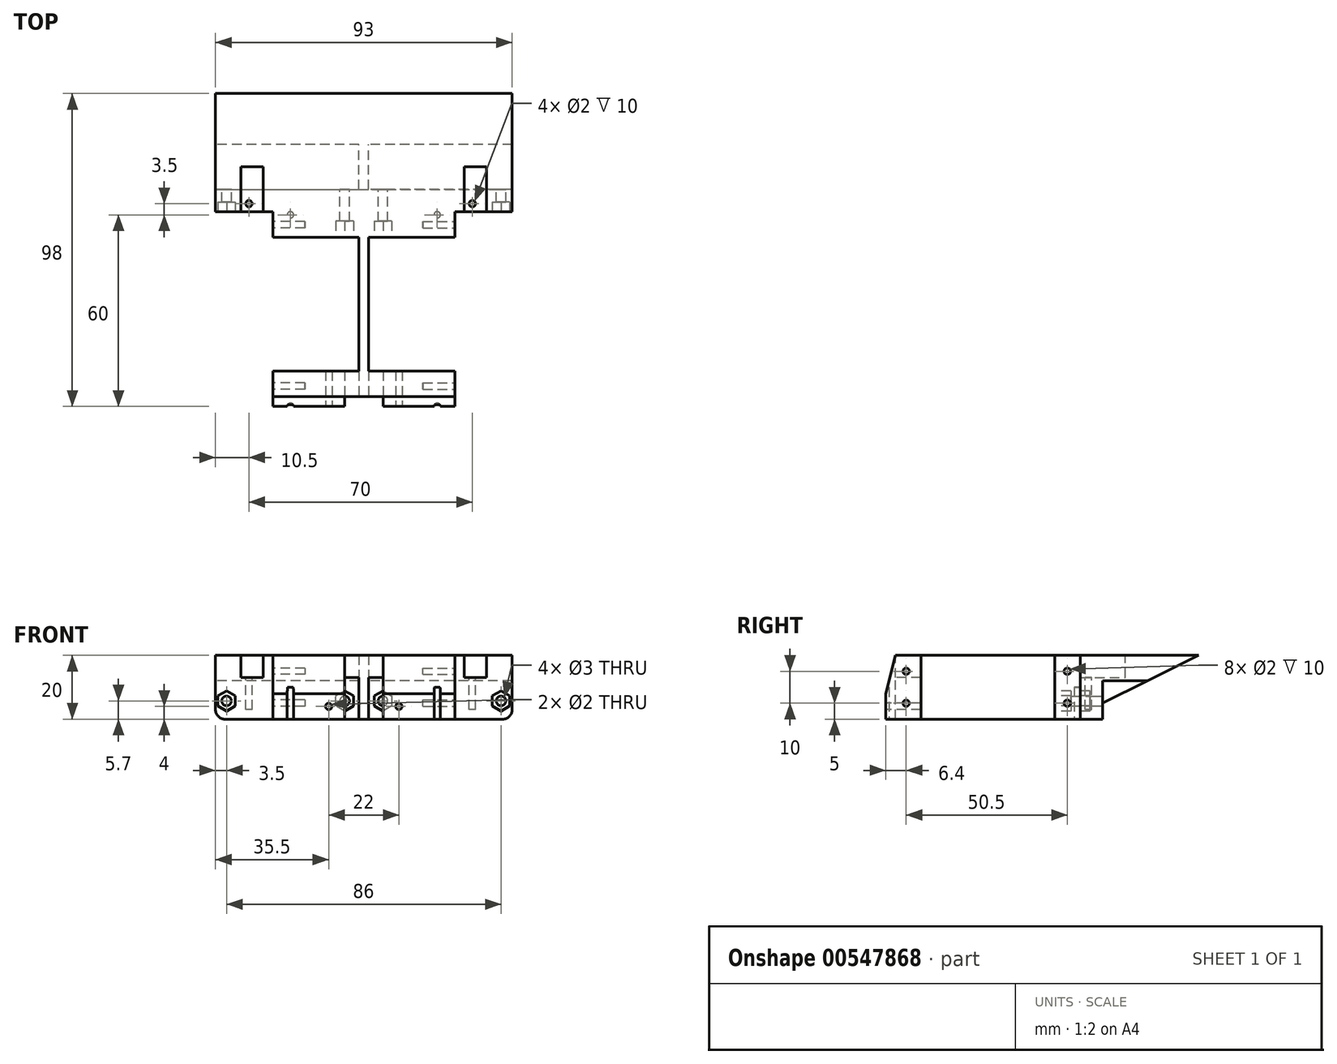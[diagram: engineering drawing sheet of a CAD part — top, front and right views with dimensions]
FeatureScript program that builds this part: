
annotation { "Feature Type Name" : "Feature", "Feature Type Description" : "" }
export const myFeature = defineFeature(function(context is Context, id is Id, definition is map)
    precondition{}
    {
        {
            var Q0;
            Q0=qCreatedBy(makeId("Top.planeOp"),FACE);
            var sketch = newSketch(context, id + "F0", { "sketchPlane" : qUnion([Q0])});
            skLineSegment(sketch, "E0", {"start": v(0, 0) * mm, "end": v(0, 8) * mm});
            skLineSegment(sketch, "E1", {"start": v(0, 8) * mm, "end": v(27, 8) * mm});
            skLineSegment(sketch, "E2", {"start": v(27, 8) * mm, "end": v(27, 50) * mm});
            skLineSegment(sketch, "E3", {"start": v(27, 50) * mm, "end": v(0, 50) * mm});
            skLineSegment(sketch, "E4", {"start": v(0, 50) * mm, "end": v(0, 65) * mm});
            skLineSegment(sketch, "E5", {"start": v(0, 65) * mm, "end": v(57, 65) * mm});
            skLineSegment(sketch, "E6", {"start": v(57, 65) * mm, "end": v(57, 50) * mm});
            skLineSegment(sketch, "E7", {"start": v(57, 50) * mm, "end": v(30, 50) * mm});
            skLineSegment(sketch, "E8", {"start": v(30, 50) * mm, "end": v(30, 8) * mm});
            skLineSegment(sketch, "E9", {"start": v(30, 8) * mm, "end": v(57, 8) * mm});
            skLineSegment(sketch, "E10", {"start": v(57, 8) * mm, "end": v(57, 0) * mm});
            skLineSegment(sketch, "E11", {"start": v(57, 0) * mm, "end": v(0, 0) * mm});
            skSolve(sketch);
        }
        {
            var Q0;
            Q0=makeQuery(id+"F0.imprint","IMPRINT",FACE,{"disambiguationData":[TD([[makeQuery(id+"F0.imprint","IMPRINT",EDGE,{"derivedFrom":sQuery(id+"F0.wireOp",EDGE,"E0")}),-1.0]])]});
            extrude(context, id + "F1", {"entities" : qUnion([Q0]), "depth" : 20 * mm, "offsetDistance" : 25 * mm});
        }
        {
            var Q0;
            Q0=makeQuery(id+"F1.opExtrude","SWEPT_FACE",FACE,{"disambiguationData":[OSD([sQuery(id+"F0.wireOp",EDGE,"E10")])]});
            var sketch = newSketch(context, id + "F2", { "sketchPlane" : qUnion([Q0])});
            skCircle(sketch, "E12", {"center": v(3.4, 15) * mm, "radius": 1 * mm});
            skCircle(sketch, "E13", {"center": v(3.4, 5) * mm, "radius": 1 * mm});
            skCircle(sketch, "E14", {"center": v(53.9, 15) * mm, "radius": 1 * mm});
            skCircle(sketch, "E15", {"center": v(53.9, 5) * mm, "radius": 1 * mm});
            skLineSegment(sketch, "E16", {"start": v(53.9, 5) * mm, "end": v(3.4, 5) * mm, "construction": true});
            skLineSegment(sketch, "E17", {"start": v(53.9, 5) * mm, "end": v(53.9, 15) * mm, "construction": true});
            skLineSegment(sketch, "E18", {"start": v(3.4, 5) * mm, "end": v(3.4, 15) * mm, "construction": true});
            skSolve(sketch);
        }
        {
            var Q0;
            Q0=makeQuery(id+"F2.imprint","IMPRINT",FACE,{"disambiguationData":[TD([[makeQuery(id+"F2.imprint","IMPRINT",EDGE,{"derivedFrom":sQuery(id+"F2.wireOp",EDGE,"E12")}),1.0]])]});
            var Q1;
            Q1=makeQuery(id+"F2.imprint","IMPRINT",FACE,{"disambiguationData":[TD([[makeQuery(id+"F2.imprint","IMPRINT",EDGE,{"derivedFrom":sQuery(id+"F2.wireOp",EDGE,"E13")}),1.0]])]});
            var Q2;
            Q2=makeQuery(id+"F2.imprint","IMPRINT",FACE,{"disambiguationData":[TD([[makeQuery(id+"F2.imprint","IMPRINT",EDGE,{"derivedFrom":sQuery(id+"F2.wireOp",EDGE,"E14")}),1.0]])]});
            var Q3;
            Q3=makeQuery(id+"F2.imprint","IMPRINT",FACE,{"disambiguationData":[TD([[makeQuery(id+"F2.imprint","IMPRINT",EDGE,{"derivedFrom":sQuery(id+"F2.wireOp",EDGE,"E15")}),1.0]])]});
            extrude(context, id + "F3", {"entities" : qUnion([Q0, Q1, Q2, Q3]), "operationType" : NewBodyOperationType.REMOVE, "oppositeDirection" : true, "depth" : 10 * mm, "offsetDistance" : 25 * mm});
        }
        {
            var Q0;
            Q0=makeQuery(id+"F1.opExtrude","SWEPT_FACE",FACE,{"disambiguationData":[OSD([sQuery(id+"F0.wireOp",EDGE,"E4")])]});
            var sketch = newSketch(context, id + "F4", { "sketchPlane" : qUnion([Q0])});
            skCircle(sketch, "E19", {"center": v(-53.9, 15) * mm, "radius": 1 * mm});
            skCircle(sketch, "E20", {"center": v(-53.9, 5) * mm, "radius": 1 * mm});
            skCircle(sketch, "E21", {"center": v(-3.4, 15) * mm, "radius": 1 * mm});
            skCircle(sketch, "E22", {"center": v(-3.4, 5) * mm, "radius": 1 * mm});
            skSolve(sketch);
        }
        {
            var Q0;
            Q0=makeQuery(id+"F4.imprint","IMPRINT",FACE,{"disambiguationData":[TD([[makeQuery(id+"F4.imprint","IMPRINT",EDGE,{"derivedFrom":sQuery(id+"F4.wireOp",EDGE,"E19")}),1.0]])]});
            var Q1;
            Q1=makeQuery(id+"F4.imprint","IMPRINT",FACE,{"disambiguationData":[TD([[makeQuery(id+"F4.imprint","IMPRINT",EDGE,{"derivedFrom":sQuery(id+"F4.wireOp",EDGE,"E20")}),1.0]])]});
            var Q2;
            Q2=makeQuery(id+"F4.imprint","IMPRINT",FACE,{"disambiguationData":[TD([[makeQuery(id+"F4.imprint","IMPRINT",EDGE,{"derivedFrom":sQuery(id+"F4.wireOp",EDGE,"E21")}),1.0]])]});
            var Q3;
            Q3=makeQuery(id+"F4.imprint","IMPRINT",FACE,{"disambiguationData":[TD([[makeQuery(id+"F4.imprint","IMPRINT",EDGE,{"derivedFrom":sQuery(id+"F4.wireOp",EDGE,"E22")}),1.0]])]});
            extrude(context, id + "F5", {"entities" : qUnion([Q0, Q1, Q2, Q3]), "operationType" : NewBodyOperationType.REMOVE, "oppositeDirection" : true, "depth" : 10 * mm, "offsetDistance" : 25 * mm});
        }
        {
            var Q0;
            Q0=makeQuery(id+"F1.opExtrude","SWEPT_FACE",FACE,{"disambiguationData":[OSD([sQuery(id+"F0.wireOp",EDGE,"E6")])]});
            var sketch = newSketch(context, id + "F6", { "sketchPlane" : qUnion([Q0])});
            skLineSegment(sketch, "E23", {"start": v(65, 5) * mm, "end": v(95, 20) * mm});
            skLineSegment(sketch, "E24", {"start": v(95, 20) * mm, "end": v(65, 20) * mm});
            skLineSegment(sketch, "E25", {"start": v(65, 20) * mm, "end": v(65, 5) * mm});
            skSolve(sketch);
        }
        {
            var Q0;
            Q0=makeQuery(id+"F6.imprint","IMPRINT",FACE,{"disambiguationData":[TD([[makeQuery(id+"F6.imprint","IMPRINT",EDGE,{"derivedFrom":sQuery(id+"F6.wireOp",EDGE,"E23")}),1.0]])]});
            var Q1;
            Q1=makeQuery(id+"F1.opExtrude","SWEPT_FACE",FACE,{"disambiguationData":[OSD([sQuery(id+"F0.wireOp",EDGE,"E4")])]});
            extrude(context, id + "F7", {"entities" : qUnion([Q0]), "operationType" : NewBodyOperationType.ADD, "oppositeDirection" : true, "depth" : 75 * mm, "endBoundEntityFace" : qUnion([Q1]), "offsetDistance" : 25 * mm, "hasSecondDirection" : true, "secondDirectionOppositeDirection" : true, "secondDirectionDepth" : -18 * mm});
        }
        {
            var Q0;
            Q0=makeQuery(id+"F1.opExtrude","SWEPT_FACE",FACE,{"disambiguationData":[OSD([sQuery(id+"F0.wireOp",EDGE,"E11")])]});
            var sketch = newSketch(context, id + "F8", { "sketchPlane" : qUnion([Q0])});
            skLineSegment(sketch, "E26.bottom", {"start": v(27, 13) * mm, "end": v(22.5, 13) * mm});
            skLineSegment(sketch, "E27", {"start": v(28.5, 0) * mm, "end": v(28.5, 20) * mm, "construction": true});
            skLineSegment(sketch, "E28", {"start": v(18, 10) * mm, "end": v(28.5, 10) * mm, "construction": true});
            skLineSegment(sketch, "E29", {"start": v(22.5, 7) * mm, "end": v(22.5, 0) * mm});
            skLineSegment(sketch, "E30", {"start": v(22.5, 0) * mm, "end": v(27, 0) * mm});
            skLineSegment(sketch, "E31", {"start": v(27, 0) * mm, "end": v(27, 13) * mm});
            skLineSegment(sketch, "E32.MirrorCS", {"start": v(34.5, 7) * mm, "end": v(34.5, 0) * mm});
            skLineSegment(sketch, "E33.MirrorCS", {"start": v(34.5, 0) * mm, "end": v(30, 0) * mm});
            skLineSegment(sketch, "E34.MirrorCS", {"start": v(30, 0) * mm, "end": v(30, 13) * mm});
            skLineSegment(sketch, "E35.MirrorCS", {"start": v(30, 13) * mm, "end": v(34.5, 13) * mm});
            skLineSegment(sketch, "E36", {"start": v(34.5, 7) * mm, "end": v(34.5, 13) * mm});
            skLineSegment(sketch, "E37", {"start": v(22.5, 13) * mm, "end": v(22.5, 7) * mm});
            skPoint(sketch, "E38.orphan", {"position": v(18, 7) * mm});
            skPoint(sketch, "E26.right.start.orphan", {"position": v(18, 13) * mm});
            skPoint(sketch, "E39.orphan", {"position": v(39, 13) * mm});
            skPoint(sketch, "E40.MirrorCS.end.orphan", {"position": v(39, 7) * mm});
            skPoint(sketch, "E41.MirrorCS.start.orphan", {"position": v(34.5, 7) * mm});
            skSolve(sketch);
        }
        {
            var Q0;
            Q0=makeQuery(id+"F8.imprint","IMPRINT",FACE,{"disambiguationData":[TD([[makeQuery(id+"F8.imprint","IMPRINT",EDGE,{"derivedFrom":sQuery(id+"F8.wireOp",EDGE,"E26.bottom")}),1.0]])]});
            var Q1;
            Q1=makeQuery(id+"F8.imprint","IMPRINT",FACE,{"disambiguationData":[TD([[makeQuery(id+"F8.imprint","IMPRINT",EDGE,{"derivedFrom":sQuery(id+"F8.wireOp",EDGE,"E32.MirrorCS")}),-1.0]])]});
            extrude(context, id + "F9", {"entities" : qUnion([Q0, Q1]), "operationType" : NewBodyOperationType.REMOVE, "oppositeDirection" : true, "depth" : 12 * mm, "offsetDistance" : 25 * mm});
        }
        {
            var Q0;
            Q0=makeQuery(id+"F1.opExtrude","CAP_FACE",FACE,{"disambiguationData":[OSD([sQuery(id+"F0.wireOp",EDGE,"E0"),sQuery(id+"F0.wireOp",EDGE,"E1"),sQuery(id+"F0.wireOp",EDGE,"E2"),sQuery(id+"F0.wireOp",EDGE,"E3"),sQuery(id+"F0.wireOp",EDGE,"E4"),sQuery(id+"F0.wireOp",EDGE,"E5"),sQuery(id+"F0.wireOp",EDGE,"E6"),sQuery(id+"F0.wireOp",EDGE,"E7"),sQuery(id+"F0.wireOp",EDGE,"E8"),sQuery(id+"F0.wireOp",EDGE,"E9"),sQuery(id+"F0.wireOp",EDGE,"E10"),sQuery(id+"F0.wireOp",EDGE,"E11")])],"isStart":true});
            var sketch = newSketch(context, id + "F10", { "sketchPlane" : qUnion([Q0])});
            skLineSegment(sketch, "E42", {"start": v(30, -65) * mm, "end": v(30, -105) * mm});
            skLineSegment(sketch, "E43", {"start": v(30, -105) * mm, "end": v(80, -105) * mm});
            skLineSegment(sketch, "E44", {"start": v(80, -105) * mm, "end": v(80, -65) * mm});
            skLineSegment(sketch, "E45", {"start": v(80, -65) * mm, "end": v(30, -65) * mm});
            skLineSegment(sketch, "E46", {"start": v(27, -50) * mm, "end": v(30, -50) * mm, "construction": true});
            skLineSegment(sketch, "E47", {"start": v(28.5, -50) * mm, "end": v(28.5, -54.4) * mm, "construction": true});
            skLineSegment(sketch, "E48.MirrorCS", {"start": v(27, -65) * mm, "end": v(27, -105) * mm});
            skLineSegment(sketch, "E49.MirrorCS", {"start": v(-23, -65) * mm, "end": v(27, -65) * mm});
            skLineSegment(sketch, "E50.MirrorCS", {"start": v(-23, -105) * mm, "end": v(-23, -65) * mm});
            skLineSegment(sketch, "E51.MirrorCS", {"start": v(27, -105) * mm, "end": v(-23, -105) * mm});
            skSolve(sketch);
        }
        {
            var Q0;
            {var subQ3=sQuery(id+"F10.wireOp",EDGE,"E48.MirrorCS");Q0=makeQuery(id+"F10.imprint","IMPRINT",FACE,{"disambiguationData":[TD([[makeQuery(id+"F10.imprint","IMPRINT",EDGE,{"derivedFrom":subQ3}),-1.0]])]});}
            var Q1;
            {var subQ4=sQuery(id+"F10.wireOp",EDGE,"E42");Q1=makeQuery(id+"F10.imprint","IMPRINT",FACE,{"disambiguationData":[TD([[makeQuery(id+"F10.imprint","IMPRINT",EDGE,{"derivedFrom":subQ4}),1.0]])]});}
            extrude(context, id + "F11", {"entities" : qUnion([Q0, Q1]), "operationType" : NewBodyOperationType.REMOVE, "oppositeDirection" : true, "depth" : 12 * mm, "offsetDistance" : 25 * mm});
        }
        {
            var Q0;
            Q0=makeQuery(id+"F11.boolean.opBoolean","MERGE",FACE,{"derivedFrom":[makeQuery(id+"F1.opExtrude","SWEPT_FACE",FACE,{"disambiguationData":[OSD([sQuery(id+"F0.wireOp",EDGE,"E5")])]}),makeQuery(id+"F11.opExtrude","SWEPT_FACE",FACE,{"disambiguationData":[OSD([sQuery(id+"F10.wireOp",EDGE,"E45")])]}),makeQuery(id+"F11.opExtrude","SWEPT_FACE",FACE,{"disambiguationData":[OSD([sQuery(id+"F10.wireOp",EDGE,"E49.MirrorCS")])]})]});
            var sketch = newSketch(context, id + "F12", { "sketchPlane" : qUnion([Q0])});
            skLineSegment(sketch, "E52", {"start": v(-75, 0) * mm, "end": v(-75, 20) * mm});
            skLineSegment(sketch, "E53", {"start": v(-75, 20) * mm, "end": v(-57, 20) * mm});
            skLineSegment(sketch, "E54", {"start": v(-57, 20) * mm, "end": v(-57, 0) * mm});
            skLineSegment(sketch, "E55", {"start": v(-57, 0) * mm, "end": v(0, 0) * mm, "construction": true});
            skLineSegment(sketch, "E56", {"start": v(-28.5, 0) * mm, "end": v(-28.5, 25.91) * mm, "construction": true});
            skLineSegment(sketch, "E57", {"start": v(-57, 0) * mm, "end": v(-75, 0) * mm});
            skLineSegment(sketch, "E58.MirrorCS", {"start": v(0, 0) * mm, "end": v(18, 0) * mm});
            skLineSegment(sketch, "E59.MirrorCS", {"start": v(0, 20) * mm, "end": v(0, 0) * mm});
            skLineSegment(sketch, "E60.MirrorCS", {"start": v(18, 20) * mm, "end": v(0, 20) * mm});
            skLineSegment(sketch, "E61.MirrorCS", {"start": v(18, 0) * mm, "end": v(18, 20) * mm});
            skSolve(sketch);
        }
        {
            var Q0;
            Q0=makeQuery(id+"F12.imprint","IMPRINT",FACE,{"disambiguationData":[TD([[makeQuery(id+"F12.imprint","IMPRINT",EDGE,{"derivedFrom":sQuery(id+"F12.wireOp",EDGE,"E52")}),-1.0]])]});
            var Q1;
            Q1=makeQuery(id+"F12.imprint","IMPRINT",FACE,{"disambiguationData":[TD([[makeQuery(id+"F12.imprint","IMPRINT",EDGE,{"derivedFrom":sQuery(id+"F12.wireOp",EDGE,"E58.MirrorCS")}),1.0]])]});
            extrude(context, id + "F13", {"entities" : qUnion([Q0, Q1]), "operationType" : NewBodyOperationType.ADD, "oppositeDirection" : true, "depth" : 7 * mm, "offsetDistance" : 25 * mm});
        }
        {
            var Q0;
            Q0=makeQuery(id+"F13.boolean.opBoolean","MERGE",FACE,{"derivedFrom":[makeQuery(id+"FaigYpugeFjXcMo_1.boolean.opBoolean","MERGE",FACE,{"derivedFrom":[makeQuery(id+"F11.boolean.opBoolean","COPY",FACE,{"derivedFrom":makeQuery(id+"F11.opExtrude","SWEPT_FACE",FACE,{"disambiguationData":[OSD([sQuery(id+"F10.wireOp",EDGE,"E45")])]})}),makeQuery(id+"FaigYpugeFjXcMo_1.opExtrude","SWEPT_FACE",FACE,{"disambiguationData":[OSD([sQuery(id+"Fybsm6U9hBihCkf_1.wireOp",EDGE,"Q4yo8pTs-f2aV-JBux-9yHL-tDEv9YkHMdLA.bottom")])]})]}),makeQuery(id+"F13.opExtrude","CAP_FACE",FACE,{"disambiguationData":[OSD([sQuery(id+"F12.wireOp",EDGE,"E52"),sQuery(id+"F12.wireOp",EDGE,"E53"),sQuery(id+"F12.wireOp",EDGE,"E54"),sQuery(id+"F12.wireOp",EDGE,"E57")])],"isStart":true})]});
            var sketch = newSketch(context, id + "F14", { "sketchPlane" : qUnion([Q0])});
            skCircle(sketch, "E62", {"center": v(-71.5, 5.7) * mm, "radius": 1.5 * mm});
            skLineSegment(sketch, "E63", {"start": v(-71.5, 5.7) * mm, "end": v(-34.5, 5.7) * mm, "construction": true});
            skCircle(sketch, "E64", {"center": v(-34.5, 5.7) * mm, "radius": 1.5 * mm});
            skLineSegment(sketch, "E65", {"start": v(-75, 0) * mm, "end": v(18, 0) * mm, "construction": true});
            skLineSegment(sketch, "E66", {"start": v(-28.5, 0) * mm, "end": v(-28.5, -6.25) * mm, "construction": true});
            skCircle(sketch, "E67.MirrorC", {"center": v(-22.5, 5.7) * mm, "radius": 1.5 * mm});
            skCircle(sketch, "E68.MirrorC", {"center": v(14.5, 5.7) * mm, "radius": 1.5 * mm});
            skSolve(sketch);
        }
        {
            var Q0;
            Q0 = qSketchRegion(id + "F14", true);
            extrude(context, id + "F15", {"entities" : qUnion([Q0]), "operationType" : NewBodyOperationType.REMOVE, "oppositeDirection" : true, "depth" : 25 * mm, "offsetDistance" : 25 * mm});
        }
        {
            var Q0;
            Q0=makeQuery(id+"F13.opExtrude","SWEPT_EDGE",EDGE,{"disambiguationData":[OSD([sQuery(id+"F12.wireOp",EDGE,"E52"),sQuery(id+"F12.wireOp",EDGE,"E57")])]});
            var Q1;
            Q1=makeQuery(id+"F13.opExtrude","SWEPT_EDGE",EDGE,{"disambiguationData":[OSD([sQuery(id+"F12.wireOp",EDGE,"E58.MirrorCS"),sQuery(id+"F12.wireOp",EDGE,"E61.MirrorCS")])]});
            fillet(context, id + "F16", {"entities" : qUnion([Q0, Q1]), "radius" : 3 * mm, "tangentPropagation" : true, "allowEdgeOverflow" : false});
        }
        {
            var Q0;
            Q0=makeQuery(id+"F1.opExtrude","SWEPT_FACE",FACE,{"disambiguationData":[OSD([sQuery(id+"F0.wireOp",EDGE,"E10")])]});
            var sketch = newSketch(context, id + "F17", { "sketchPlane" : qUnion([Q0])});
            skLineSegment(sketch, "E69", {"start": v(-3, 0) * mm, "end": v(0, 0) * mm});
            skLineSegment(sketch, "E70", {"start": v(0, 0) * mm, "end": v(0, 20) * mm});
            skLineSegment(sketch, "E71", {"start": v(-3, 0) * mm, "end": v(-3, 8) * mm});
            skLineSegment(sketch, "E72", {"start": v(-3, 8) * mm, "end": v(0, 20) * mm});
            skSolve(sketch);
        }
        {
            var Q0;
            Q0 = qSketchRegion(id + "F17", true);
            var Q1;
            Q1=makeQuery(id+"F9.boolean.opBoolean","COPY",FACE,{"derivedFrom":makeQuery(id+"F9.opExtrude","SWEPT_FACE",FACE,{"disambiguationData":[OSD([sQuery(id+"F8.wireOp",EDGE,"E32.MirrorCS"),sQuery(id+"F8.wireOp",EDGE,"E36")])]})});
            extrude(context, id + "F18", {"entities" : qUnion([Q0]), "operationType" : NewBodyOperationType.ADD, "endBound" : BoundingType.UP_TO_SURFACE, "oppositeDirection" : true, "depth" : 25 * mm, "endBoundEntityFace" : qUnion([Q1]), "offsetDistance" : 25 * mm});
        }
        {
            var Q0;
            Q0=makeQuery(id+"F1.opExtrude","SWEPT_FACE",FACE,{"disambiguationData":[OSD([sQuery(id+"F0.wireOp",EDGE,"E0")])]});
            var sketch = newSketch(context, id + "F19", { "sketchPlane" : qUnion([Q0])});
            skLineSegment(sketch, "E73", {"start": v(3, 0) * mm, "end": v(0, 0) * mm});
            skLineSegment(sketch, "E74", {"start": v(0, 0) * mm, "end": v(0, 20) * mm});
            skLineSegment(sketch, "E75", {"start": v(3, 0) * mm, "end": v(3, 8) * mm});
            skLineSegment(sketch, "E76", {"start": v(3, 8) * mm, "end": v(0, 20) * mm});
            skSolve(sketch);
        }
        {
            var Q0;
            Q0=makeQuery(id+"F19.imprint","IMPRINT",FACE,{"disambiguationData":[TD([[makeQuery(id+"F19.imprint","IMPRINT",EDGE,{"derivedFrom":sQuery(id+"F19.wireOp",EDGE,"E73")}),-1.0]])]});
            var Q1;
            Q1=makeQuery(id+"F9.boolean.opBoolean","COPY",FACE,{"derivedFrom":makeQuery(id+"F9.opExtrude","SWEPT_FACE",FACE,{"disambiguationData":[OSD([sQuery(id+"F8.wireOp",EDGE,"E29"),sQuery(id+"F8.wireOp",EDGE,"E37")])]})});
            extrude(context, id + "F20", {"entities" : qUnion([Q0]), "operationType" : NewBodyOperationType.ADD, "endBound" : BoundingType.UP_TO_SURFACE, "oppositeDirection" : true, "depth" : 25 * mm, "endBoundEntityFace" : qUnion([Q1]), "offsetDistance" : 25 * mm});
        }
        {
            var Q0;
            {var subQ0=sQuery(id+"F0.wireOp",EDGE,"E5");var subQ1=sQuery(id+"F0.wireOp",EDGE,"E4");var subQ2=sQuery(id+"F0.wireOp",EDGE,"E3");var subQ3=sQuery(id+"F0.wireOp",EDGE,"E2");var subQ4=sQuery(id+"F0.wireOp",EDGE,"E6");var subQ5=sQuery(id+"F0.wireOp",EDGE,"E7");var subQ6=sQuery(id+"F0.wireOp",EDGE,"E8");var subQ7=sQuery(id+"F0.wireOp",EDGE,"E11");Q0=makeQuery(id+"F13.boolean.opBoolean","MERGE",FACE,{"derivedFrom":[makeQuery(id+"F9.boolean.opBoolean","SPLIT",FACE,{"disambiguationData":[TD([makeQuery(id+"F1.opExtrude","SWEPT_FACE",FACE,{"disambiguationData":[OSD([subQ3])]})])],"derivedFrom":makeQuery(id+"F1.opExtrude","CAP_FACE",FACE,{"disambiguationData":[OSD([sQuery(id+"F0.wireOp",EDGE,"E0"),sQuery(id+"F0.wireOp",EDGE,"E1"),subQ3,subQ2,subQ1,subQ0,subQ4,subQ5,subQ6,sQuery(id+"F0.wireOp",EDGE,"E9"),sQuery(id+"F0.wireOp",EDGE,"E10"),subQ7])],"isStart":true})}),makeQuery(id+"F13.opExtrude","SWEPT_FACE",FACE,{"disambiguationData":[OSD([sQuery(id+"F12.wireOp",EDGE,"E57")])]}),makeQuery(id+"F13.opExtrude","SWEPT_FACE",FACE,{"disambiguationData":[OSD([sQuery(id+"F12.wireOp",EDGE,"E58.MirrorCS")])]})]});}
            var sketch = newSketch(context, id + "F21", { "sketchPlane" : qUnion([Q0])});
            skLineSegment(sketch, "E77.bottom", {"start": v(51.5, 3) * mm, "end": v(5.5, 3) * mm, "construction": true});
            skLineSegment(sketch, "E77.top", {"start": v(51.5, -57) * mm, "end": v(5.5, -57) * mm, "construction": true});
            skCircle(sketch, "E78", {"center": v(5.5, -57) * mm, "radius": 1 * mm});
            skCircle(sketch, "E79", {"center": v(5.5, 3) * mm, "radius": 1 * mm});
            skCircle(sketch, "E80", {"center": v(51.5, 3) * mm, "radius": 1 * mm});
            skCircle(sketch, "E81", {"center": v(51.5, -57) * mm, "radius": 1 * mm});
            skLineSegment(sketch, "E82", {"start": v(28.5, 3) * mm, "end": v(28.5, 0) * mm, "construction": true});
            skLineSegment(sketch, "E83", {"start": v(28.5, 3) * mm, "end": v(28.5, -57) * mm, "construction": true});
            skSolve(sketch);
        }
        {
            var Q0;
            Q0 = qSketchRegion(id + "F21", true);
            extrude(context, id + "F22", {"entities" : qUnion([Q0]), "operationType" : NewBodyOperationType.REMOVE, "oppositeDirection" : true, "depth" : 10 * mm, "offsetDistance" : 25 * mm});
        }
        {
            var Q0;
            Q0=makeQuery(id+"F13.boolean.opBoolean","MERGE",FACE,{"derivedFrom":[makeQuery(id+"F7.boolean.opBoolean","MERGE",FACE,{"derivedFrom":[makeQuery(id+"F1.opExtrude","CAP_FACE",FACE,{"disambiguationData":[OSD([sQuery(id+"F0.wireOp",EDGE,"E0"),sQuery(id+"F0.wireOp",EDGE,"E1"),sQuery(id+"F0.wireOp",EDGE,"E2"),sQuery(id+"F0.wireOp",EDGE,"E3"),sQuery(id+"F0.wireOp",EDGE,"E4"),sQuery(id+"F0.wireOp",EDGE,"E5"),sQuery(id+"F0.wireOp",EDGE,"E6"),sQuery(id+"F0.wireOp",EDGE,"E7"),sQuery(id+"F0.wireOp",EDGE,"E8"),sQuery(id+"F0.wireOp",EDGE,"E9"),sQuery(id+"F0.wireOp",EDGE,"E10"),sQuery(id+"F0.wireOp",EDGE,"E11")])],"isStart":false}),makeQuery(id+"F7.opExtrude","SWEPT_FACE",FACE,{"disambiguationData":[OSD([sQuery(id+"F6.wireOp",EDGE,"E24")])]})]}),makeQuery(id+"F13.opExtrude","SWEPT_FACE",FACE,{"disambiguationData":[OSD([sQuery(id+"F12.wireOp",EDGE,"E53")])]}),makeQuery(id+"F13.opExtrude","SWEPT_FACE",FACE,{"disambiguationData":[OSD([sQuery(id+"F12.wireOp",EDGE,"E60.MirrorCS")])]})]});
            var sketch = newSketch(context, id + "F23", { "sketchPlane" : qUnion([Q0])});
            skLineSegment(sketch, "E84.bottom", {"start": v(-10, 58) * mm, "end": v(-3, 58) * mm});
            skLineSegment(sketch, "E84.top", {"start": v(-10, 72) * mm, "end": v(-3, 72) * mm});
            skLineSegment(sketch, "E84.left", {"start": v(-10, 58) * mm, "end": v(-10, 72) * mm});
            skLineSegment(sketch, "E84.right", {"start": v(-3, 58) * mm, "end": v(-3, 72) * mm});
            skLineSegment(sketch, "E85", {"start": v(28.5, 95) * mm, "end": v(28.5, 59.92) * mm, "construction": true});
            skLineSegment(sketch, "E86.MirrorCS", {"start": v(67, 58) * mm, "end": v(60, 58) * mm});
            skLineSegment(sketch, "E87.MirrorCS", {"start": v(67, 58) * mm, "end": v(67, 72) * mm});
            skLineSegment(sketch, "E88.MirrorCS", {"start": v(67, 72) * mm, "end": v(60, 72) * mm});
            skLineSegment(sketch, "E89.MirrorCS", {"start": v(60, 58) * mm, "end": v(60, 72) * mm});
            skSolve(sketch);
        }
        {
            var Q0;
            Q0=makeQuery(id+"F23.imprint","IMPRINT",FACE,{"disambiguationData":[TD([[makeQuery(id+"F23.imprint","IMPRINT",EDGE,{"derivedFrom":sQuery(id+"F23.wireOp",EDGE,"E84.bottom")}),1.0]])]});
            var Q1;
            Q1=makeQuery(id+"F23.imprint","IMPRINT",FACE,{"disambiguationData":[TD([[makeQuery(id+"F23.imprint","IMPRINT",EDGE,{"derivedFrom":sQuery(id+"F23.wireOp",EDGE,"E86.MirrorCS")}),-1.0]])]});
            extrude(context, id + "F24", {"entities" : qUnion([Q0, Q1]), "operationType" : NewBodyOperationType.REMOVE, "oppositeDirection" : true, "depth" : 7 * mm, "offsetDistance" : 25 * mm});
        }
        {
            var Q0;
            Q0=makeQuery(id+"F18.opExtrude","SWEPT_FACE",FACE,{"disambiguationData":[OSD([sQuery(id+"F17.wireOp",EDGE,"E71")])]});
            var sketch = newSketch(context, id + "F25", { "sketchPlane" : qUnion([Q0])});
            skCircle(sketch, "E90", {"center": v(39.5, 4) * mm, "radius": 1 * mm});
            skCircle(sketch, "E91", {"center": v(17.5, 4) * mm, "radius": 1 * mm});
            skLineSegment(sketch, "E92", {"start": v(17.5, 4) * mm, "end": v(39.5, 4) * mm, "construction": true});
            skSolve(sketch);
        }
        {
            var Q0;
            Q0=makeQuery(id+"F25.imprint","IMPRINT",FACE,{"disambiguationData":[TD([[makeQuery(id+"F25.imprint","IMPRINT",EDGE,{"derivedFrom":sQuery(id+"F25.wireOp",EDGE,"E91")}),1.0]])]});
            var Q1;
            Q1=makeQuery(id+"F25.imprint","IMPRINT",FACE,{"disambiguationData":[TD([[makeQuery(id+"F25.imprint","IMPRINT",EDGE,{"derivedFrom":sQuery(id+"F25.wireOp",EDGE,"E90")}),1.0]])]});
            extrude(context, id + "F26", {"entities" : qUnion([Q0, Q1]), "operationType" : NewBodyOperationType.REMOVE, "oppositeDirection" : true, "depth" : 25 * mm, "offsetDistance" : 25 * mm});
        }
        {
            var Q0;
            Q0=makeQuery(id+"F24.boolean.opBoolean","COPY",FACE,{"derivedFrom":makeQuery(id+"F24.opExtrude","CAP_FACE",FACE,{"disambiguationData":[OSD([sQuery(id+"F23.wireOp",EDGE,"E86.MirrorCS"),sQuery(id+"F23.wireOp",EDGE,"E87.MirrorCS"),sQuery(id+"F23.wireOp",EDGE,"E88.MirrorCS"),sQuery(id+"F23.wireOp",EDGE,"E89.MirrorCS")])],"isStart":false})});
            var sketch = newSketch(context, id + "F27", { "sketchPlane" : qUnion([Q0])});
            skCircle(sketch, "E93", {"center": v(-7.5, 60.5) * mm, "radius": 1 * mm});
            skCircle(sketch, "E94", {"center": v(62.5, 60.5) * mm, "radius": 1 * mm});
            skSolve(sketch);
        }
        {
            var Q0;
            Q0=makeQuery(id+"F27.imprint","IMPRINT",FACE,{"disambiguationData":[TD([[makeQuery(id+"F27.imprint","IMPRINT",EDGE,{"derivedFrom":sQuery(id+"F27.wireOp",EDGE,"E93")}),1.0]])]});
            var Q1;
            Q1=makeQuery(id+"F27.imprint","IMPRINT",FACE,{"disambiguationData":[TD([[makeQuery(id+"F27.imprint","IMPRINT",EDGE,{"derivedFrom":sQuery(id+"F27.wireOp",EDGE,"E94")}),1.0]])]});
            extrude(context, id + "F28", {"entities" : qUnion([Q0, Q1]), "operationType" : NewBodyOperationType.REMOVE, "oppositeDirection" : true, "depth" : 10 * mm, "offsetDistance" : 25 * mm});
        }
        {
            var Q0;
            Q0=makeQuery(id+"F1.opExtrude","SWEPT_FACE",FACE,{"disambiguationData":[OSD([sQuery(id+"F0.wireOp",EDGE,"E7")])]});
            var sketch = newSketch(context, id + "F29", { "sketchPlane" : qUnion([Q0])});
            skCircle(sketch, "E95.cCircle", {"center": v(34.5, 5.7) * mm, "radius": 2.75 * mm, "construction": true});
            skLineSegment(sketch, "E95.0", {"start": v(37.25, 4.11) * mm, "end": v(34.5, 2.52) * mm});
            skLineSegment(sketch, "E95.1", {"start": v(34.5, 2.52) * mm, "end": v(31.75, 4.11) * mm});
            skLineSegment(sketch, "E95.2", {"start": v(31.75, 4.11) * mm, "end": v(31.75, 7.29) * mm});
            skLineSegment(sketch, "E95.3", {"start": v(31.75, 7.29) * mm, "end": v(34.5, 8.88) * mm});
            skLineSegment(sketch, "E95.4", {"start": v(34.5, 8.88) * mm, "end": v(37.25, 7.29) * mm});
            skLineSegment(sketch, "E95.5", {"start": v(37.25, 7.29) * mm, "end": v(37.25, 4.11) * mm});
            skPoint(sketch, "E95.0.midPoint", {"position": v(35.87, 3.32) * mm});
            skLineSegment(sketch, "E96", {"start": v(34.5, 5.7) * mm, "end": v(34.5, 2.52) * mm, "construction": true});
            skSolve(sketch);
        }
        {
            var Q0;
            Q0=makeQuery(id+"F1.opExtrude","SWEPT_FACE",FACE,{"disambiguationData":[OSD([sQuery(id+"F0.wireOp",EDGE,"E3")])]});
            var sketch = newSketch(context, id + "F30", { "sketchPlane" : qUnion([Q0])});
            skCircle(sketch, "E97.cCircle", {"center": v(22.5, 5.7) * mm, "radius": 2.75 * mm, "construction": true});
            skLineSegment(sketch, "E97.0", {"start": v(19.75, 4.11) * mm, "end": v(19.75, 7.29) * mm});
            skLineSegment(sketch, "E97.1", {"start": v(19.75, 7.29) * mm, "end": v(22.5, 8.88) * mm});
            skLineSegment(sketch, "E97.2", {"start": v(22.5, 8.88) * mm, "end": v(25.25, 7.29) * mm});
            skLineSegment(sketch, "E97.3", {"start": v(25.25, 7.29) * mm, "end": v(25.25, 4.11) * mm});
            skLineSegment(sketch, "E97.4", {"start": v(25.25, 4.11) * mm, "end": v(22.5, 2.52) * mm});
            skLineSegment(sketch, "E97.5", {"start": v(22.5, 2.52) * mm, "end": v(19.75, 4.11) * mm});
            skPoint(sketch, "E97.0.midPoint", {"position": v(19.75, 5.7) * mm});
            skLineSegment(sketch, "E98", {"start": v(22.5, 5.7) * mm, "end": v(22.5, 2.52) * mm, "construction": true});
            skSolve(sketch);
        }
        {
            var Q0;
            Q0=makeQuery(id+"F13.opExtrude","CAP_FACE",FACE,{"disambiguationData":[OSD([sQuery(id+"F12.wireOp",EDGE,"E52"),sQuery(id+"F12.wireOp",EDGE,"E53"),sQuery(id+"F12.wireOp",EDGE,"E54"),sQuery(id+"F12.wireOp",EDGE,"E57")])],"isStart":false});
            var sketch = newSketch(context, id + "F31", { "sketchPlane" : qUnion([Q0])});
            skCircle(sketch, "E99.cCircle", {"center": v(71.5, 5.7) * mm, "radius": 2.75 * mm, "construction": true});
            skLineSegment(sketch, "E99.0", {"start": v(68.75, 7.29) * mm, "end": v(71.5, 8.88) * mm});
            skLineSegment(sketch, "E99.1", {"start": v(71.5, 8.88) * mm, "end": v(74.25, 7.29) * mm});
            skLineSegment(sketch, "E99.2", {"start": v(74.25, 7.29) * mm, "end": v(74.25, 4.11) * mm});
            skLineSegment(sketch, "E99.3", {"start": v(74.25, 4.11) * mm, "end": v(71.5, 2.52) * mm});
            skLineSegment(sketch, "E99.4", {"start": v(71.5, 2.52) * mm, "end": v(68.75, 4.11) * mm});
            skLineSegment(sketch, "E99.5", {"start": v(68.75, 4.11) * mm, "end": v(68.75, 7.29) * mm});
            skPoint(sketch, "E99.0.midPoint", {"position": v(70.12, 8.08) * mm});
            skLineSegment(sketch, "E100", {"start": v(71.5, 2.52) * mm, "end": v(71.5, 5.7) * mm, "construction": true});
            skSolve(sketch);
        }
        {
            var Q0;
            Q0=makeQuery(id+"F13.opExtrude","CAP_FACE",FACE,{"disambiguationData":[OSD([sQuery(id+"F12.wireOp",EDGE,"E58.MirrorCS"),sQuery(id+"F12.wireOp",EDGE,"E59.MirrorCS"),sQuery(id+"F12.wireOp",EDGE,"E60.MirrorCS"),sQuery(id+"F12.wireOp",EDGE,"E61.MirrorCS")])],"isStart":false});
            var sketch = newSketch(context, id + "F32", { "sketchPlane" : qUnion([Q0])});
            skCircle(sketch, "E101.cCircle", {"center": v(-14.5, 5.7) * mm, "radius": 2.75 * mm, "construction": true});
            skLineSegment(sketch, "E101.0", {"start": v(-11.75, 7.29) * mm, "end": v(-11.75, 4.11) * mm});
            skLineSegment(sketch, "E101.1", {"start": v(-11.75, 4.11) * mm, "end": v(-14.5, 2.52) * mm});
            skLineSegment(sketch, "E101.2", {"start": v(-14.5, 2.52) * mm, "end": v(-17.25, 4.11) * mm});
            skLineSegment(sketch, "E101.3", {"start": v(-17.25, 4.11) * mm, "end": v(-17.25, 7.29) * mm});
            skLineSegment(sketch, "E101.4", {"start": v(-17.25, 7.29) * mm, "end": v(-14.5, 8.88) * mm});
            skLineSegment(sketch, "E101.5", {"start": v(-14.5, 8.88) * mm, "end": v(-11.75, 7.29) * mm});
            skPoint(sketch, "E101.0.midPoint", {"position": v(-11.75, 5.7) * mm});
            skLineSegment(sketch, "E102", {"start": v(-14.5, 2.52) * mm, "end": v(-14.5, 5.7) * mm, "construction": true});
            skSolve(sketch);
        }
        {
            var Q0;
            Q0=makeQuery(id+"F29.imprint","IMPRINT",FACE,{"disambiguationData":[TD([[makeQuery(id+"F29.imprint","IMPRINT",EDGE,{"derivedFrom":sQuery(id+"F29.wireOp",EDGE,"E95.0")}),-1.0]])]});
            var Q1;
            Q1=makeQuery(id+"F30.imprint","IMPRINT",FACE,{"disambiguationData":[TD([[makeQuery(id+"F30.imprint","IMPRINT",EDGE,{"derivedFrom":sQuery(id+"F30.wireOp",EDGE,"E97.0")}),-1.0]])]});
            extrude(context, id + "F33", {"entities" : qUnion([Q0, Q1]), "operationType" : NewBodyOperationType.REMOVE, "oppositeDirection" : true, "depth" : 5 * mm, "offsetDistance" : 25 * mm});
        }
        {
            var Q0;
            Q0 = qSketchRegion(id + "F31", true);
            var Q1;
            Q1=makeQuery(id+"F32.imprint","IMPRINT",FACE,{"disambiguationData":[TD([[makeQuery(id+"F32.imprint","IMPRINT",EDGE,{"derivedFrom":sQuery(id+"F32.wireOp",EDGE,"E101.0")}),-1.0]])]});
            extrude(context, id + "F34", {"entities" : qUnion([Q0, Q1]), "operationType" : NewBodyOperationType.REMOVE, "oppositeDirection" : true, "depth" : 3 * mm, "offsetDistance" : 25 * mm});
        }
    });
